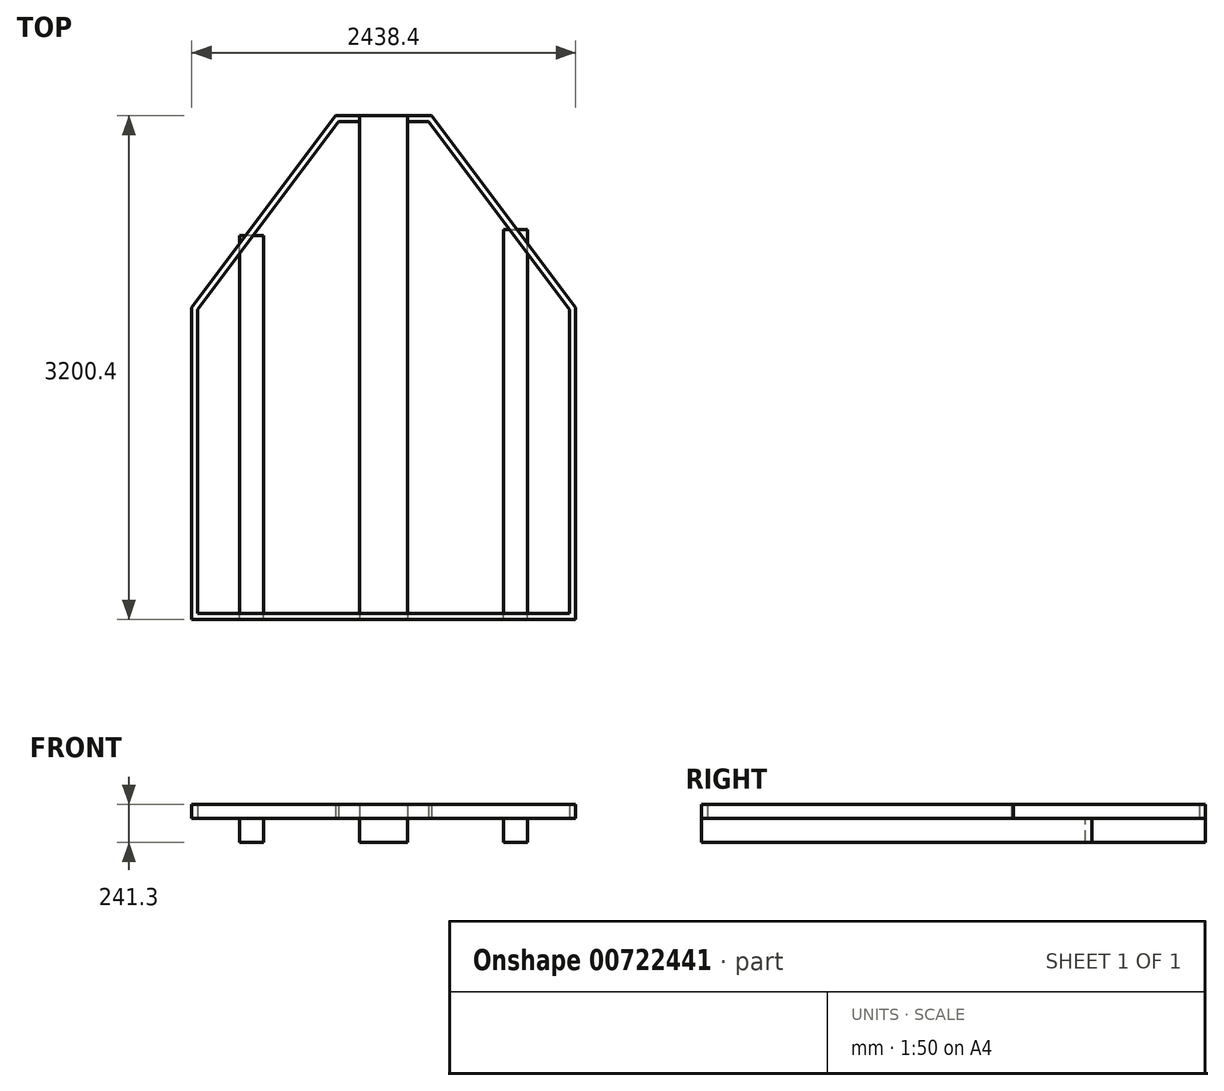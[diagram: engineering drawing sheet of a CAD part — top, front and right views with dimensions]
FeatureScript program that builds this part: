
annotation { "Feature Type Name" : "Feature", "Feature Type Description" : "" }
export const myFeature = defineFeature(function(context is Context, id is Id, definition is map)
    precondition{}
    {
        {
            var Q0;
            Q0=qCreatedBy(makeId("Top.planeOp"),FACE);
            var sketch = newSketch(context, id + "F0", { "sketchPlane" : qUnion([Q0])});
            skLineSegment(sketch, "E0.bottom", {"start": v(-501.05, 1394.7) * mm, "end": v(-196.25, 1394.7) * mm});
            skLineSegment(sketch, "E0.top", {"start": v(-501.05, -1805.7) * mm, "end": v(-196.25, -1805.7) * mm});
            skLineSegment(sketch, "E0.left", {"start": v(-501.05, 1394.7) * mm, "end": v(-501.05, -1805.7) * mm});
            skLineSegment(sketch, "E0.right", {"start": v(-196.25, 1394.7) * mm, "end": v(-196.25, -1805.7) * mm});
            skLineSegment(sketch, "E1.bottom", {"start": v(-1110.65, -1805.7) * mm, "end": v(-1263.05, -1805.7) * mm});
            skLineSegment(sketch, "E1.top", {"start": v(-1110.65, 632.7) * mm, "end": v(-1263.05, 632.7) * mm});
            skLineSegment(sketch, "E1.left", {"start": v(-1110.65, -1805.7) * mm, "end": v(-1110.65, 632.7) * mm});
            skLineSegment(sketch, "E1.right", {"start": v(-1263.05, -1805.7) * mm, "end": v(-1263.05, 632.7) * mm});
            skLineSegment(sketch, "E2.bottom", {"start": v(413.35, -1805.7) * mm, "end": v(565.75, -1805.7) * mm});
            skLineSegment(sketch, "E2.top", {"start": v(413.35, 671.77) * mm, "end": v(565.75, 671.77) * mm});
            skLineSegment(sketch, "E2.left", {"start": v(413.35, -1805.7) * mm, "end": v(413.35, 671.77) * mm});
            skLineSegment(sketch, "E2.right", {"start": v(565.75, -1805.7) * mm, "end": v(565.75, 671.77) * mm});
            skSolve(sketch);
        }
        {
            var Q0;
            Q0 = qSketchRegion(id + "F0", true);
            extrude(context, id + "F1", {"entities" : qUnion([Q0]), "oppositeDirection" : true, "depth" : 152.4 * mm, "offsetDistance" : 25.4 * mm});
        }
        {
            var Q0;
            Q0=makeQuery(id+"F1.opExtrude","CAP_FACE",FACE,{"disambiguationData":[OSD([sQuery(id+"F0.wireOp",EDGE,"E0.bottom"),sQuery(id+"F0.wireOp",EDGE,"E0.top"),sQuery(id+"F0.wireOp",EDGE,"E0.left"),sQuery(id+"F0.wireOp",EDGE,"E0.right")])],"isStart":true});
            var sketch = newSketch(context, id + "F2", { "sketchPlane" : qUnion([Q0])});
            skLineSegment(sketch, "E3", {"start": v(-348.65, -1805.7) * mm, "end": v(870.55, -1805.7) * mm});
            skLineSegment(sketch, "E4", {"start": v(870.55, -1805.7) * mm, "end": v(870.55, 175.5) * mm});
            skLineSegment(sketch, "E5.MirrorCS", {"start": v(-1567.85, -1805.7) * mm, "end": v(-1567.85, 175.5) * mm});
            skLineSegment(sketch, "E6.MirrorCS", {"start": v(-348.65, -1805.7) * mm, "end": v(-1567.85, -1805.7) * mm});
            skLineSegment(sketch, "E7", {"start": v(-348.65, -1805.7) * mm, "end": v(-348.65, 1394.7) * mm, "construction": true});
            skLineSegment(sketch, "E8", {"start": v(-1567.85, 175.5) * mm, "end": v(-653.45, 1394.7) * mm});
            skLineSegment(sketch, "E9", {"start": v(-653.45, 1394.7) * mm, "end": v(-348.65, 1394.7) * mm});
            skLineSegment(sketch, "E10", {"start": v(-348.65, 1394.7) * mm, "end": v(-43.85, 1394.7) * mm});
            skLineSegment(sketch, "E11", {"start": v(-43.85, 1394.7) * mm, "end": v(870.55, 175.5) * mm});
            skLineSegment(sketch, "E12.0", {"start": v(-348.65, -1767.6) * mm, "end": v(-1529.75, -1767.6) * mm});
            skLineSegment(sketch, "E12.1", {"start": v(-1529.75, -1767.6) * mm, "end": v(-1529.75, 162.8) * mm});
            skLineSegment(sketch, "E12.2", {"start": v(-348.65, -1767.6) * mm, "end": v(832.45, -1767.6) * mm});
            skLineSegment(sketch, "E12.3", {"start": v(-1529.75, 162.8) * mm, "end": v(-634.4, 1356.6) * mm});
            skLineSegment(sketch, "E12.4", {"start": v(832.45, -1767.6) * mm, "end": v(832.45, 162.8) * mm});
            skLineSegment(sketch, "E12.5", {"start": v(-62.9, 1356.6) * mm, "end": v(832.45, 162.8) * mm});
            skLineSegment(sketch, "E12.6", {"start": v(-348.65, 1356.6) * mm, "end": v(-62.9, 1356.6) * mm});
            skLineSegment(sketch, "E12.7", {"start": v(-634.4, 1356.6) * mm, "end": v(-348.65, 1356.6) * mm});
            skSolve(sketch);
        }
        {
            var Q0;
            {var subQ7=sQuery(id+"F2.wireOp",EDGE,"E3");var subQ9=makeQuery(id+"F1.opExtrude","CAP_EDGE",EDGE,{"disambiguationData":[OSD([sQuery(id+"F0.wireOp",EDGE,"E0.right")])],"isStart":true});var subQ11=makeQuery(id+"F2.imprint","INTERSECT",VERTEX,{"derivedFrom":[subQ9,subQ7]});Q0=makeQuery(id+"F2.imprint","IMPRINT",FACE,{"disambiguationData":[TD([[makeQuery(id+"F2.imprint","IMPRINT",EDGE,{"disambiguationData":[TD([[subQ11,1.0]])],"derivedFrom":subQ7}),1.0]])]});}
            var Q1;
            {var subQ7=sQuery(id+"F2.wireOp",EDGE,"E4");Q1=makeQuery(id+"F2.imprint","IMPRINT",FACE,{"disambiguationData":[TD([[makeQuery(id+"F2.imprint","IMPRINT",EDGE,{"derivedFrom":subQ7}),1.0]])]});}
            var Q2;
            {var subQ3=makeQuery(id+"F1.opExtrude","CAP_EDGE",EDGE,{"disambiguationData":[OSD([sQuery(id+"F0.wireOp",EDGE,"E0.left")])],"isStart":true});var subQ9=sQuery(id+"F2.wireOp",EDGE,"E9");var subQ11=makeQuery(id+"F2.imprint","INTERSECT",VERTEX,{"derivedFrom":[subQ3,subQ9]});Q2=makeQuery(id+"F2.imprint","IMPRINT",FACE,{"disambiguationData":[TD([[makeQuery(id+"F2.imprint","IMPRINT",EDGE,{"disambiguationData":[TD([[subQ11,-1.0]])],"derivedFrom":subQ9}),-1.0]])]});}
            extrude(context, id + "F3", {"entities" : qUnion([Q0, Q1, Q2]), "depth" : 88.9 * mm, "offsetDistance" : 25.4 * mm});
        }
    });
